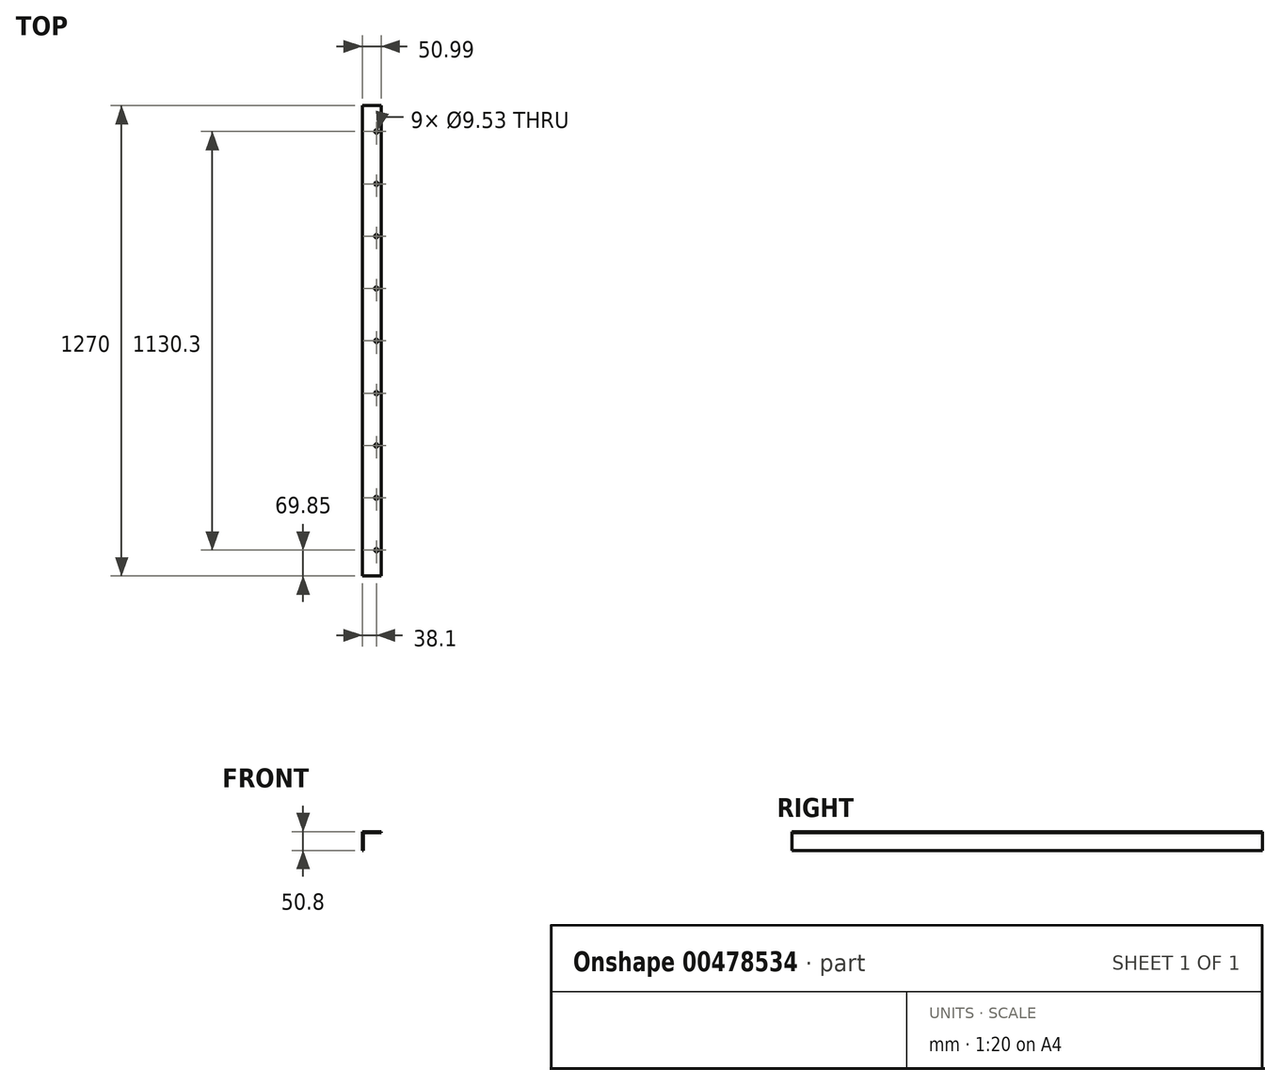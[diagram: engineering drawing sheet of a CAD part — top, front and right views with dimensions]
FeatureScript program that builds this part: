
annotation { "Feature Type Name" : "Feature", "Feature Type Description" : "" }
export const myFeature = defineFeature(function(context is Context, id is Id, definition is map)
    precondition{}
    {
        {
            var Q0;
            Q0=qCreatedBy(makeId("Front.planeOp"),FACE);
            var sketch = newSketch(context, id + "F0", { "sketchPlane" : qUnion([Q0])});
            skLineSegment(sketch, "E0", {"start": v(0, 0) * mm, "end": v(0, 50.8) * mm});
            skLineSegment(sketch, "E1", {"start": v(0, 50.8) * mm, "end": v(50.8, 50.8) * mm});
            skLineSegment(sketch, "E2", {"start": v(50.8, 50.8) * mm, "end": v(50.99, 47.63) * mm});
            skLineSegment(sketch, "E3", {"start": v(50.99, 47.63) * mm, "end": v(6.35, 47.63) * mm});
            skLineSegment(sketch, "E4", {"start": v(3.17, 44.45) * mm, "end": v(3.18, 0) * mm});
            skLineSegment(sketch, "E5", {"start": v(3.18, 0) * mm, "end": v(0, 0) * mm});
            skPoint(sketch, "E6.visualSharp", {"position": v(3.17, 47.62) * mm});
            skArc(sketch, "E6.filletArc", {"start": v(6.35, 47.63) * mm, "mid": v(4.1, 46.7) * mm, "end": v(3.17, 44.45) * mm});
            skSolve(sketch);
        }
        {
            var Q0;
            Q0=makeQuery(id+"F0.imprint","IMPRINT",FACE,{"disambiguationData":[TD([[makeQuery(id+"F0.imprint","IMPRINT",EDGE,{"derivedFrom":sQuery(id+"F0.wireOp",EDGE,"E0")}),-1.0]])]});
            extrude(context, id + "F1", {"entities" : qUnion([Q0]), "depth" : 1270 * mm});
        }
        {
            var Q0;
            Q0=makeQuery(id+"F1.opExtrude","SWEPT_FACE",FACE,{"disambiguationData":[OSD([sQuery(id+"F0.wireOp",EDGE,"E1")])]});
            var sketch = newSketch(context, id + "F2", { "sketchPlane" : qUnion([Q0])});
            skPoint(sketch, "E7", {"position": v(38.1, -69.85) * mm});
            skPoint(sketch, "E8", {"position": v(38.1, -211.14) * mm});
            skPoint(sketch, "E9", {"position": v(38.1, -352.43) * mm});
            skPoint(sketch, "E10", {"position": v(38.1, -493.71) * mm});
            skPoint(sketch, "E11", {"position": v(38.1, -635) * mm});
            skPoint(sketch, "E12", {"position": v(38.1, -776.29) * mm});
            skPoint(sketch, "E13", {"position": v(38.1, -917.58) * mm});
            skPoint(sketch, "E14", {"position": v(38.1, -1058.86) * mm});
            skCircle(sketch, "E15", {"center": v(38.1, -69.85) * mm, "radius": 4.76 * mm});
            skCircle(sketch, "E16", {"center": v(38.1, -211.14) * mm, "radius": 4.76 * mm});
            skCircle(sketch, "E17", {"center": v(38.1, -352.43) * mm, "radius": 4.76 * mm});
            skCircle(sketch, "E18", {"center": v(38.1, -493.71) * mm, "radius": 4.76 * mm});
            skCircle(sketch, "E19", {"center": v(38.1, -635) * mm, "radius": 4.76 * mm});
            skCircle(sketch, "E20", {"center": v(38.1, -776.29) * mm, "radius": 4.76 * mm});
            skCircle(sketch, "E21", {"center": v(38.1, -917.58) * mm, "radius": 4.76 * mm});
            skCircle(sketch, "E22", {"center": v(38.1, -1058.86) * mm, "radius": 4.76 * mm});
            skLineSegment(sketch, "E23", {"start": v(38.1, -1058.86) * mm, "end": v(38.1, -917.58) * mm});
            skLineSegment(sketch, "E24", {"start": v(38.1, -917.58) * mm, "end": v(38.1, -776.29) * mm});
            skLineSegment(sketch, "E25", {"start": v(38.1, -635) * mm, "end": v(38.1, -776.29) * mm});
            skLineSegment(sketch, "E26", {"start": v(38.1, -635) * mm, "end": v(38.1, -493.71) * mm});
            skLineSegment(sketch, "E27", {"start": v(38.1, -493.71) * mm, "end": v(38.1, -352.43) * mm});
            skLineSegment(sketch, "E28", {"start": v(38.1, -211.14) * mm, "end": v(38.1, -352.43) * mm});
            skLineSegment(sketch, "E29", {"start": v(38.1, -211.14) * mm, "end": v(38.1, -69.85) * mm});
            skPoint(sketch, "E30", {"position": v(38.1, -1200.15) * mm});
            skCircle(sketch, "E31", {"center": v(38.1, -1200.15) * mm, "radius": 4.76 * mm});
            skLineSegment(sketch, "E32", {"start": v(38.1, -1200.15) * mm, "end": v(38.1, -1058.86) * mm});
            skSolve(sketch);
        }
        {
            var Q0;
            Q0=makeQuery(id+"F2.imprint","IMPRINT",FACE,{"disambiguationData":[TD([[makeQuery(id+"F2.imprint","IMPRINT",EDGE,{"derivedFrom":sQuery(id+"F2.wireOp",EDGE,"E15")}),1.0]])]});
            var Q1;
            {var subQ0=sQuery(id+"F2.wireOp",EDGE,"E28");var subQ1=sQuery(id+"F2.wireOp",EDGE,"E16");var subQ2=makeQuery(id+"F2.imprint","INTERSECT",VERTEX,{"derivedFrom":[subQ1,subQ0]});Q1=makeQuery(id+"F2.imprint","IMPRINT",FACE,{"disambiguationData":[TD([[makeQuery(id+"F2.imprint","IMPRINT",EDGE,{"disambiguationData":[TD([[subQ2,-1.0]])],"derivedFrom":subQ1}),1.0]])]});}
            var Q2;
            {var subQ0=sQuery(id+"F2.wireOp",EDGE,"E28");var subQ1=sQuery(id+"F2.wireOp",EDGE,"E16");var subQ2=makeQuery(id+"F2.imprint","INTERSECT",VERTEX,{"derivedFrom":[subQ1,subQ0]});Q2=makeQuery(id+"F2.imprint","IMPRINT",FACE,{"disambiguationData":[TD([[makeQuery(id+"F2.imprint","IMPRINT",EDGE,{"disambiguationData":[TD([[subQ2,1.0]])],"derivedFrom":subQ1}),1.0]])]});}
            var Q3;
            {var subQ0=sQuery(id+"F2.wireOp",EDGE,"E27");var subQ1=sQuery(id+"F2.wireOp",EDGE,"E17");var subQ2=makeQuery(id+"F2.imprint","INTERSECT",VERTEX,{"derivedFrom":[subQ1,subQ0]});Q3=makeQuery(id+"F2.imprint","IMPRINT",FACE,{"disambiguationData":[TD([[makeQuery(id+"F2.imprint","IMPRINT",EDGE,{"disambiguationData":[TD([[subQ2,-1.0]])],"derivedFrom":subQ1}),1.0]])]});}
            var Q4;
            {var subQ0=sQuery(id+"F2.wireOp",EDGE,"E26");var subQ1=sQuery(id+"F2.wireOp",EDGE,"E18");var subQ2=makeQuery(id+"F2.imprint","INTERSECT",VERTEX,{"derivedFrom":[subQ1,subQ0]});Q4=makeQuery(id+"F2.imprint","IMPRINT",FACE,{"disambiguationData":[TD([[makeQuery(id+"F2.imprint","IMPRINT",EDGE,{"disambiguationData":[TD([[subQ2,-1.0]])],"derivedFrom":subQ1}),1.0]])]});}
            var Q5;
            {var subQ0=sQuery(id+"F2.wireOp",EDGE,"E26");var subQ1=sQuery(id+"F2.wireOp",EDGE,"E18");var subQ2=makeQuery(id+"F2.imprint","INTERSECT",VERTEX,{"derivedFrom":[subQ1,subQ0]});Q5=makeQuery(id+"F2.imprint","IMPRINT",FACE,{"disambiguationData":[TD([[makeQuery(id+"F2.imprint","IMPRINT",EDGE,{"disambiguationData":[TD([[subQ2,1.0]])],"derivedFrom":subQ1}),1.0]])]});}
            var Q6;
            {var subQ0=sQuery(id+"F2.wireOp",EDGE,"E24");var subQ1=sQuery(id+"F2.wireOp",EDGE,"E20");var subQ2=makeQuery(id+"F2.imprint","INTERSECT",VERTEX,{"derivedFrom":[subQ1,subQ0]});Q6=makeQuery(id+"F2.imprint","IMPRINT",FACE,{"disambiguationData":[TD([[makeQuery(id+"F2.imprint","IMPRINT",EDGE,{"disambiguationData":[TD([[subQ2,-1.0]])],"derivedFrom":subQ1}),1.0]])]});}
            var Q7;
            {var subQ0=sQuery(id+"F2.wireOp",EDGE,"E24");var subQ1=sQuery(id+"F2.wireOp",EDGE,"E20");var subQ2=makeQuery(id+"F2.imprint","INTERSECT",VERTEX,{"derivedFrom":[subQ1,subQ0]});Q7=makeQuery(id+"F2.imprint","IMPRINT",FACE,{"disambiguationData":[TD([[makeQuery(id+"F2.imprint","IMPRINT",EDGE,{"disambiguationData":[TD([[subQ2,1.0]])],"derivedFrom":subQ1}),1.0]])]});}
            var Q8;
            {var subQ0=sQuery(id+"F2.wireOp",EDGE,"E25");var subQ1=sQuery(id+"F2.wireOp",EDGE,"E19");var subQ2=makeQuery(id+"F2.imprint","INTERSECT",VERTEX,{"derivedFrom":[subQ1,subQ0]});Q8=makeQuery(id+"F2.imprint","IMPRINT",FACE,{"disambiguationData":[TD([[makeQuery(id+"F2.imprint","IMPRINT",EDGE,{"disambiguationData":[TD([[subQ2,-1.0]])],"derivedFrom":subQ1}),1.0]])]});}
            var Q9;
            {var subQ0=sQuery(id+"F2.wireOp",EDGE,"E25");var subQ1=sQuery(id+"F2.wireOp",EDGE,"E19");var subQ2=makeQuery(id+"F2.imprint","INTERSECT",VERTEX,{"derivedFrom":[subQ1,subQ0]});Q9=makeQuery(id+"F2.imprint","IMPRINT",FACE,{"disambiguationData":[TD([[makeQuery(id+"F2.imprint","IMPRINT",EDGE,{"disambiguationData":[TD([[subQ2,1.0]])],"derivedFrom":subQ1}),1.0]])]});}
            var Q10;
            {var subQ0=sQuery(id+"F2.wireOp",EDGE,"E23");var subQ1=sQuery(id+"F2.wireOp",EDGE,"E21");var subQ2=makeQuery(id+"F2.imprint","INTERSECT",VERTEX,{"derivedFrom":[subQ1,subQ0]});Q10=makeQuery(id+"F2.imprint","IMPRINT",FACE,{"disambiguationData":[TD([[makeQuery(id+"F2.imprint","IMPRINT",EDGE,{"disambiguationData":[TD([[subQ2,-1.0]])],"derivedFrom":subQ1}),1.0]])]});}
            var Q11;
            {var subQ0=sQuery(id+"F2.wireOp",EDGE,"E23");var subQ1=sQuery(id+"F2.wireOp",EDGE,"E21");var subQ2=makeQuery(id+"F2.imprint","INTERSECT",VERTEX,{"derivedFrom":[subQ1,subQ0]});Q11=makeQuery(id+"F2.imprint","IMPRINT",FACE,{"disambiguationData":[TD([[makeQuery(id+"F2.imprint","IMPRINT",EDGE,{"disambiguationData":[TD([[subQ2,1.0]])],"derivedFrom":subQ1}),1.0]])]});}
            var Q12;
            Q12=makeQuery(id+"F2.imprint","IMPRINT",FACE,{"disambiguationData":[TD([[makeQuery(id+"F2.imprint","IMPRINT",EDGE,{"derivedFrom":sQuery(id+"F2.wireOp",EDGE,"E22")}),1.0]])]});
            var Q13;
            Q13=makeQuery(id+"F2.imprint","IMPRINT",FACE,{"disambiguationData":[TD([[makeQuery(id+"F2.imprint","IMPRINT",EDGE,{"derivedFrom":sQuery(id+"F2.wireOp",EDGE,"E31")}),1.0]])]});
            var Q14;
            {var subQ0=sQuery(id+"F2.wireOp",EDGE,"E27");var subQ1=sQuery(id+"F2.wireOp",EDGE,"E17");var subQ2=makeQuery(id+"F2.imprint","INTERSECT",VERTEX,{"derivedFrom":[subQ1,subQ0]});Q14=makeQuery(id+"F2.imprint","IMPRINT",FACE,{"disambiguationData":[TD([[makeQuery(id+"F2.imprint","IMPRINT",EDGE,{"disambiguationData":[TD([[subQ2,1.0]])],"derivedFrom":subQ1}),1.0]])]});}
            extrude(context, id + "F3", {"entities" : qUnion([Q0, Q1, Q2, Q3, Q4, Q5, Q6, Q7, Q8, Q9, Q10, Q11, Q12, Q13, Q14]), "operationType" : NewBodyOperationType.REMOVE, "endBound" : BoundingType.THROUGH_ALL, "oppositeDirection" : true, "depth" : 25.4 * mm});
        }
    });
